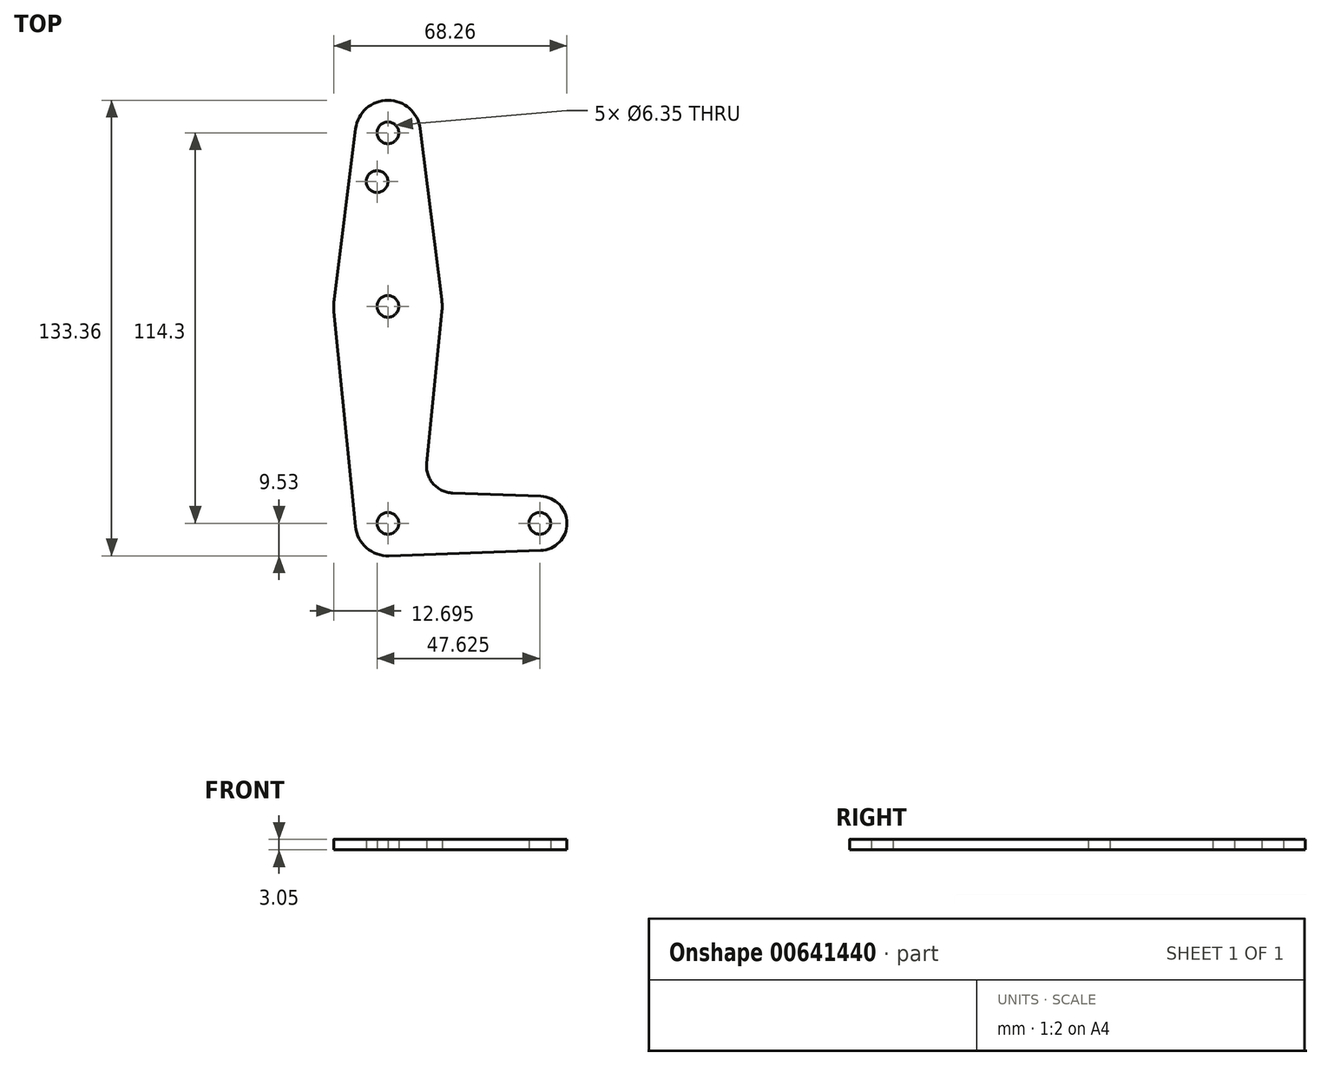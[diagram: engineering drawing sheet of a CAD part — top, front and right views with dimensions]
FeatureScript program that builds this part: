
annotation { "Feature Type Name" : "Feature", "Feature Type Description" : "" }
export const myFeature = defineFeature(function(context is Context, id is Id, definition is map)
    precondition{}
    {
        {
            var Q0;
            Q0=qCreatedBy(makeId("Top.planeOp"),FACE);
            var sketch = newSketch(context, id + "F0", { "sketchPlane" : qUnion([Q0])});
            skLineSegment(sketch, "E0", {"start": v(0, 0) * mm, "end": v(0, 114.3) * mm, "construction": true});
            skArc(sketch, "E1", {"start": v(9.45, 115.5) * mm, "mid": v(0, 123.83) * mm, "end": v(-9.45, 115.5) * mm});
            skArc(sketch, "E2", {"start": v(-9.48, -0.95) * mm, "mid": v(-6.26, -7.18) * mm, "end": v(0.34, -9.52) * mm});
            skArc(sketch, "E3", {"start": v(-15.75, 65.48) * mm, "mid": v(-15.87, 63.7) * mm, "end": v(-15.8, 61.91) * mm});
            skLineSegment(sketch, "E4", {"start": v(0, 0) * mm, "end": v(44.45, 0) * mm, "construction": true});
            skArc(sketch, "E5", {"start": v(44.73, -7.93) * mm, "mid": v(52.39, 0) * mm, "end": v(44.73, 7.93) * mm});
            skLineSegment(sketch, "E6", {"start": v(-15.8, 61.91) * mm, "end": v(-9.48, -0.95) * mm});
            skLineSegment(sketch, "E7", {"start": v(18.97, 8.85) * mm, "end": v(44.73, 7.93) * mm});
            skLineSegment(sketch, "E8", {"start": v(0.34, -9.52) * mm, "end": v(44.73, -7.93) * mm});
            skLineSegment(sketch, "E9", {"start": v(-9.45, 115.5) * mm, "end": v(-15.75, 65.48) * mm});
            skLineSegment(sketch, "E10", {"start": v(9.45, 115.5) * mm, "end": v(15.75, 65.48) * mm});
            skLineSegment(sketch, "E11", {"start": v(15.8, 61.91) * mm, "end": v(11.34, 17.6) * mm});
            skArc(sketch, "E12.filletArc", {"start": v(11.34, 17.6) * mm, "mid": v(13.26, 11.57) * mm, "end": v(18.97, 8.85) * mm});
            skCircle(sketch, "E13", {"center": v(0, 114.3) * mm, "radius": 3.18 * mm});
            skCircle(sketch, "E14", {"center": v(0, 63.5) * mm, "radius": 3.18 * mm});
            skCircle(sketch, "E15", {"center": v(0, 0) * mm, "radius": 3.18 * mm});
            skCircle(sketch, "E16", {"center": v(44.45, 0) * mm, "radius": 3.18 * mm});
            skCircle(sketch, "E17", {"center": v(-3.18, 100.03) * mm, "radius": 3.18 * mm});
            skArc(sketch, "E18.trimOffspring", {"start": v(15.8, 61.91) * mm, "mid": v(15.87, 63.7) * mm, "end": v(15.75, 65.48) * mm});
            skSolve(sketch);
        }
        {
            var Q0;
            Q0=makeQuery(id+"F0.imprint","IMPRINT",FACE,{"disambiguationData":[TD([[makeQuery(id+"F0.imprint","IMPRINT",EDGE,{"derivedFrom":sQuery(id+"F0.wireOp",EDGE,"E1")}),1.0]])]});
            extrude(context, id + "F1", {"entities" : qUnion([Q0]), "depth" : 3.05 * mm, "offsetDistance" : 25.4 * mm});
        }
    });
